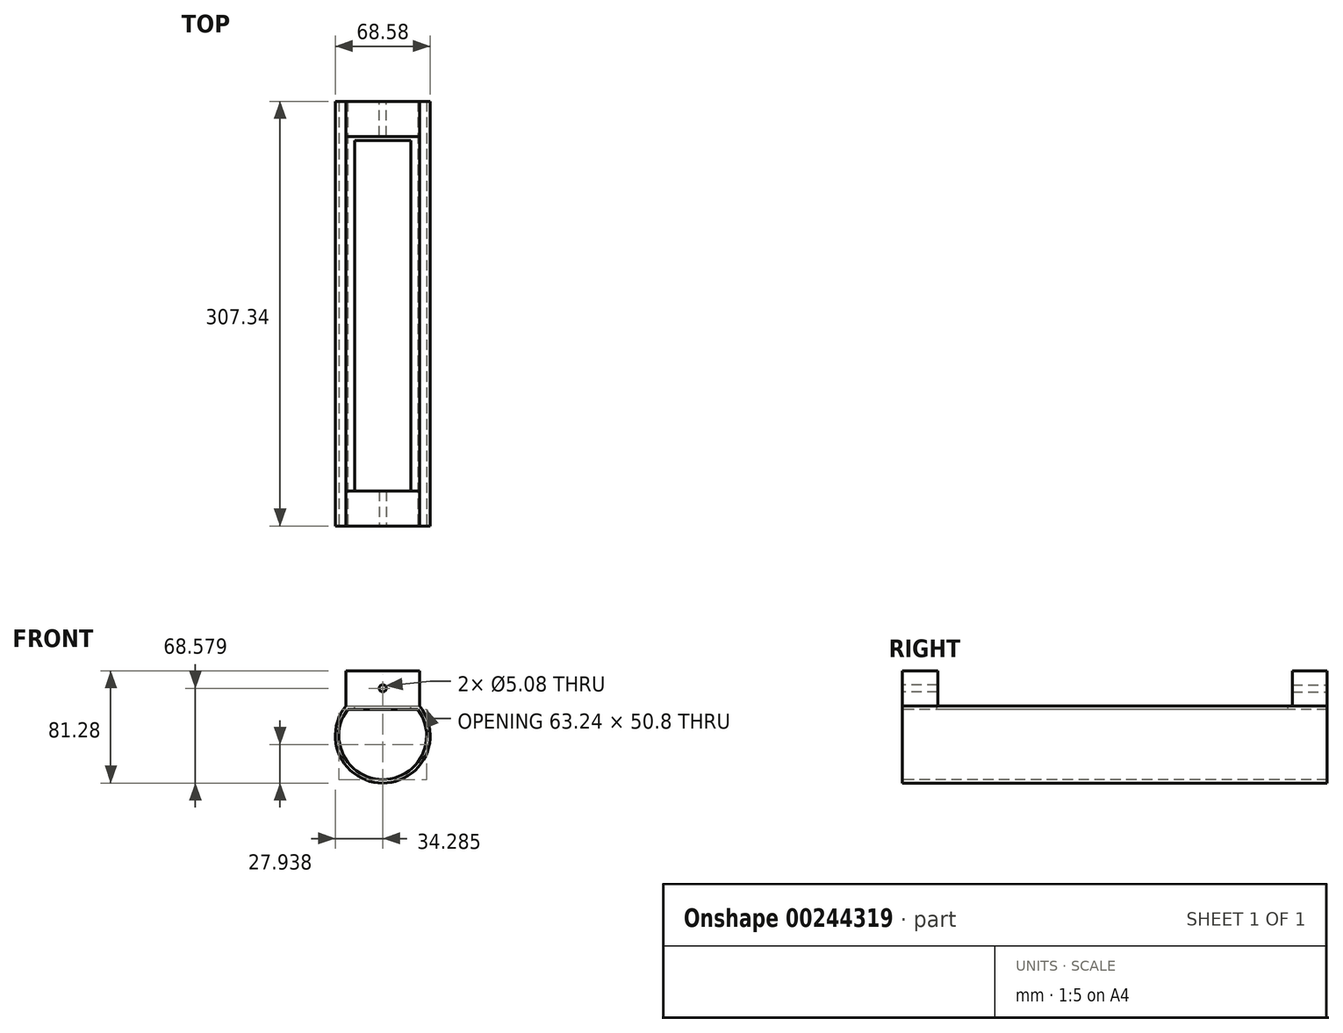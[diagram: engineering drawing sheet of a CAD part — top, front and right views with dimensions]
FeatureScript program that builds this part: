
annotation { "Feature Type Name" : "Feature", "Feature Type Description" : "" }
export const myFeature = defineFeature(function(context is Context, id is Id, definition is map)
    precondition{}
    {
        {
            var Q0;
            Q0=qCreatedBy(makeId("Front.planeOp"),FACE);
            var sketch = newSketch(context, id + "F0", { "sketchPlane" : qUnion([Q0])});
            skLineSegment(sketch, "E0", {"start": v(-30.24, 13.36) * mm, "end": v(20.55, 13.36) * mm});
            skArc(sketch, "E1", {"start": v(-30.24, 13.36) * mm, "mid": v(-4.84, -37.44) * mm, "end": v(20.55, 13.36) * mm});
            skLineSegment(sketch, "E2", {"start": v(-36.56, -7.25) * mm, "end": v(26.87, -7.25) * mm});
            skSolve(sketch);
        }
        {
            var Q0;
            Q0 = qSketchRegion(id + "F0", true);
            extrude(context, id + "F1", {"entities" : qUnion([Q0]), "oppositeDirection" : true, "depth" : 304.8 * mm});
        }
        {
            var Q0;
            Q0=makeQuery(id+"F1.opExtrude","CAP_FACE",FACE,{"disambiguationData":[OSD([sQuery(id+"F0.wireOp",EDGE,"E0"),sQuery(id+"F0.wireOp",EDGE,"E1")])],"isStart":true});
            shell(context, id + "F2", {"entities" : qUnion([Q0]), "thickness" : 2.54 * mm, "oppositeDirection" : true});
        }
        {
            var Q0;
            Q0=makeQuery(id+"F2.opShell","OFFSET_FACE",FACE,{"disambiguationData":[OSD([sQuery(id+"F0.wireOp",EDGE,"E0"),sQuery(id+"F0.wireOp",EDGE,"E1")])]});
            extrude(context, id + "F3", {"entities" : qUnion([Q0]), "operationType" : NewBodyOperationType.REMOVE, "oppositeDirection" : true, "depth" : 304.8 * mm});
        }
        {
            var Q0;
            Q0=makeQuery(id+"F1.opExtrude","SWEPT_FACE",FACE,{"disambiguationData":[OSD([sQuery(id+"F0.wireOp",EDGE,"E0")])]});
            var sketch = newSketch(context, id + "F4", { "sketchPlane" : qUnion([Q0])});
            skLineSegment(sketch, "E3", {"start": v(-25.13, 278.97) * mm, "end": v(15.5, 278.97) * mm});
            skLineSegment(sketch, "E4", {"start": v(15.5, 278.97) * mm, "end": v(15.5, 24.97) * mm});
            skLineSegment(sketch, "E5", {"start": v(-25.13, 278.97) * mm, "end": v(-25.13, 24.97) * mm});
            skLineSegment(sketch, "E6", {"start": v(-25.13, 24.97) * mm, "end": v(15.5, 24.97) * mm});
            skSolve(sketch);
        }
        {
            var Q0;
            Q0=makeQuery(id+"F4.imprint","IMPRINT",FACE,{"disambiguationData":[TD([[makeQuery(id+"F4.imprint","IMPRINT",EDGE,{"derivedFrom":sQuery(id+"F4.wireOp",EDGE,"E3")}),-1.0]])]});
            var Q1;
            Q1=sQuery(id+"F4.wireOp",EDGE,"E5");
            var Q2;
            Q2=sQuery(id+"F4.wireOp",EDGE,"E3");
            var Q3;
            Q3=sQuery(id+"F4.wireOp",EDGE,"E4");
            var Q4;
            Q4=sQuery(id+"F4.wireOp",EDGE,"E6");
            extrude(context, id + "F5", {"entities" : qUnion([Q0]), "operationType" : NewBodyOperationType.REMOVE, "surfaceEntities" : qUnion([Q1, Q2, Q3, Q4]), "endBound" : BoundingType.UP_TO_NEXT, "oppositeDirection" : true, "depth" : 25.4 * mm});
        }
        {
            var Q0;
            Q0=makeQuery(id+"F1.opExtrude","SWEPT_BODY",BODY,{"disambiguationData":[OSD([sQuery(id+"F0.wireOp",EDGE,"E0"),sQuery(id+"F0.wireOp",EDGE,"E1")])]});
            var Q1;
            Q1=qCreatedBy(makeId("Origin.pointOp"),VERTEX);
            var Q2;
            Q2=makeQuery(id+"F1.opExtrude","CAP_FACE",FACE,{"disambiguationData":[OSD([sQuery(id+"F0.wireOp",EDGE,"E0"),sQuery(id+"F0.wireOp",EDGE,"E1")])],"isStart":true});
            transform(context, id + "F6", {"entities" : qUnion([Q0]), "transformType" : TransformType.TRANSLATION_DISTANCE, "transformDirection" : qUnion([Q1, Q2]), "distance" : 127 * mm, "makeCopy" : false});
        }
        {
            var Q0;
            Q0=makeQuery(id+"F1.opExtrude","CAP_FACE",FACE,{"disambiguationData":[OSD([sQuery(id+"F0.wireOp",EDGE,"E0"),sQuery(id+"F0.wireOp",EDGE,"E1")])],"isStart":true});
            var sketch = newSketch(context, id + "F7", { "sketchPlane" : qUnion([Q0])});
            skLineSegment(sketch, "E7", {"start": v(-31.48, 15.9) * mm, "end": v(-31.48, 41.3) * mm});
            skLineSegment(sketch, "E8", {"start": v(-31.48, 41.3) * mm, "end": v(21.8, 41.3) * mm});
            skLineSegment(sketch, "E9", {"start": v(21.8, 41.3) * mm, "end": v(21.8, 15.9) * mm});
            skLineSegment(sketch, "E10", {"start": v(-4.84, 41.3) * mm, "end": v(-4.84, 15.9) * mm, "construction": true});
            skSolve(sketch);
        }
        {
            var Q0;
            Q0 = qSketchRegion(id + "F7", true);
            var Q1;
            Q1=makeQuery(id+"F7.imprint","IMPRINT",FACE,{"disambiguationData":[TD([[makeQuery(id+"F7.imprint","IMPRINT",EDGE,{"derivedFrom":sQuery(id+"F7.wireOp",EDGE,"E7")}),-1.0]])]});
            extrude(context, id + "F8", {"entities" : qUnion([Q0, Q1]), "operationType" : NewBodyOperationType.ADD, "oppositeDirection" : true, "depth" : 25.4 * mm});
        }
        {
            var Q0;
            {var subQ0=sQuery(id+"F0.wireOp",EDGE,"E0");Q0=makeQuery(id+"F8.boolean.opBoolean","MERGE",FACE,{"derivedFrom":[makeQuery(id+"F1.opExtrude","CAP_FACE",FACE,{"disambiguationData":[OSD([subQ0,sQuery(id+"F0.wireOp",EDGE,"E1")])],"isStart":true}),makeQuery(id+"F8.opExtrude","CAP_FACE",FACE,{"disambiguationData":[OSD([subQ0,sQuery(id+"F7.wireOp",EDGE,"E7"),sQuery(id+"F7.wireOp",EDGE,"E8"),sQuery(id+"F7.wireOp",EDGE,"E9")])],"isStart":true})]});}
            var sketch = newSketch(context, id + "F9", { "sketchPlane" : qUnion([Q0])});
            skCircle(sketch, "E11", {"center": v(-4.84, 28.6) * mm, "radius": 2.54 * mm});
            skSolve(sketch);
        }
        {
            var Q0;
            Q0 = qSketchRegion(id + "F9", true);
            extrude(context, id + "F10", {"entities" : qUnion([Q0]), "operationType" : NewBodyOperationType.REMOVE, "endBound" : BoundingType.UP_TO_NEXT, "oppositeDirection" : true, "depth" : 25.4 * mm});
        }
        {
            var Q0;
            Q0=makeQuery(id+"F1.opExtrude","CAP_FACE",FACE,{"disambiguationData":[OSD([sQuery(id+"F0.wireOp",EDGE,"E0"),sQuery(id+"F0.wireOp",EDGE,"E1")])],"isStart":false});
            var sketch = newSketch(context, id + "F11", { "sketchPlane" : qUnion([Q0])});
            skLineSegment(sketch, "E12", {"start": v(-21.8, 15.9) * mm, "end": v(-21.8, 41.3) * mm});
            skLineSegment(sketch, "E13", {"start": v(-21.8, 41.3) * mm, "end": v(31.48, 41.3) * mm});
            skLineSegment(sketch, "E14", {"start": v(31.48, 41.3) * mm, "end": v(31.48, 15.9) * mm});
            skSolve(sketch);
        }
        {
            var Q0;
            Q0 = qSketchRegion(id + "F11", true);
            var Q1;
            Q1=makeQuery(id+"F11.imprint","IMPRINT",FACE,{"disambiguationData":[TD([[makeQuery(id+"F11.imprint","IMPRINT",EDGE,{"derivedFrom":sQuery(id+"F11.wireOp",EDGE,"E12")}),-1.0]])]});
            extrude(context, id + "F12", {"entities" : qUnion([Q0, Q1]), "operationType" : NewBodyOperationType.ADD, "oppositeDirection" : true, "depth" : 25.4 * mm});
        }
        {
            var Q0;
            {var subQ0=sQuery(id+"F0.wireOp",EDGE,"E0");Q0=makeQuery(id+"F12.boolean.opBoolean","MERGE",FACE,{"derivedFrom":[makeQuery(id+"F1.opExtrude","CAP_FACE",FACE,{"disambiguationData":[OSD([subQ0,sQuery(id+"F0.wireOp",EDGE,"E1")])],"isStart":false}),makeQuery(id+"F12.opExtrude","CAP_FACE",FACE,{"disambiguationData":[OSD([subQ0,sQuery(id+"F11.wireOp",EDGE,"E12"),sQuery(id+"F11.wireOp",EDGE,"E13"),sQuery(id+"F11.wireOp",EDGE,"E14")])],"isStart":true})]});}
            var sketch = newSketch(context, id + "F13", { "sketchPlane" : qUnion([Q0])});
            skCircle(sketch, "E15", {"center": v(4.84, 28.6) * mm, "radius": 2.54 * mm});
            skSolve(sketch);
        }
        {
            var Q0;
            Q0 = qSketchRegion(id + "F13", true);
            extrude(context, id + "F14", {"entities" : qUnion([Q0]), "operationType" : NewBodyOperationType.REMOVE, "endBound" : BoundingType.UP_TO_NEXT, "oppositeDirection" : true, "depth" : 25.4 * mm});
        }
    });
